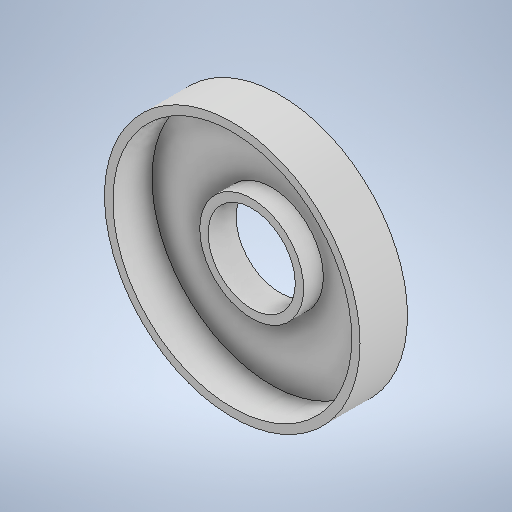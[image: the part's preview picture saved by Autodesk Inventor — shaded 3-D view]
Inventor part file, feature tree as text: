
AUTODESK INVENTOR PART (.ipt)
format: ipt  version: 2025.2 (Build 292293000, 293)  size: 266,752 bytes
history: native  units: in
note: dims shown in document units (in); Inventor stores cm internally (conversion verified against a paired STEP export)
features: extrude x4, sketch x4
ambient origin geometry x8: Origin, YZ Plane, XZ Plane, XY Plane, X Axis, Y Axis, Z Axis, Center Point
bodies: Solid1 (feature_tree)
feature tree (8):
  extrude  "Extrusion1"  Depth=0.1575in TaperAngle=0.0deg
  extrude  "Extrusion2"  Depth=0.7421in
  extrude  "Extrusion3"  Depth=0.1575in
  extrude  "Extrusion4"  Depth=0.374in
  sketch  "Sketch1"  dims[d0=4.8425in d1=0.1575in d2=0.0in]
  sketch  "Sketch2"  dims[d4=0.7421in d5=0.0in d6=1.6535in]
  sketch  "Sketch3"  dims[d7=0.0in d8=0.0in d9=0.1575in]
  sketch  "Sketch4"  dims[d10=0.374in d11=0.0in d12=4.5276in]
